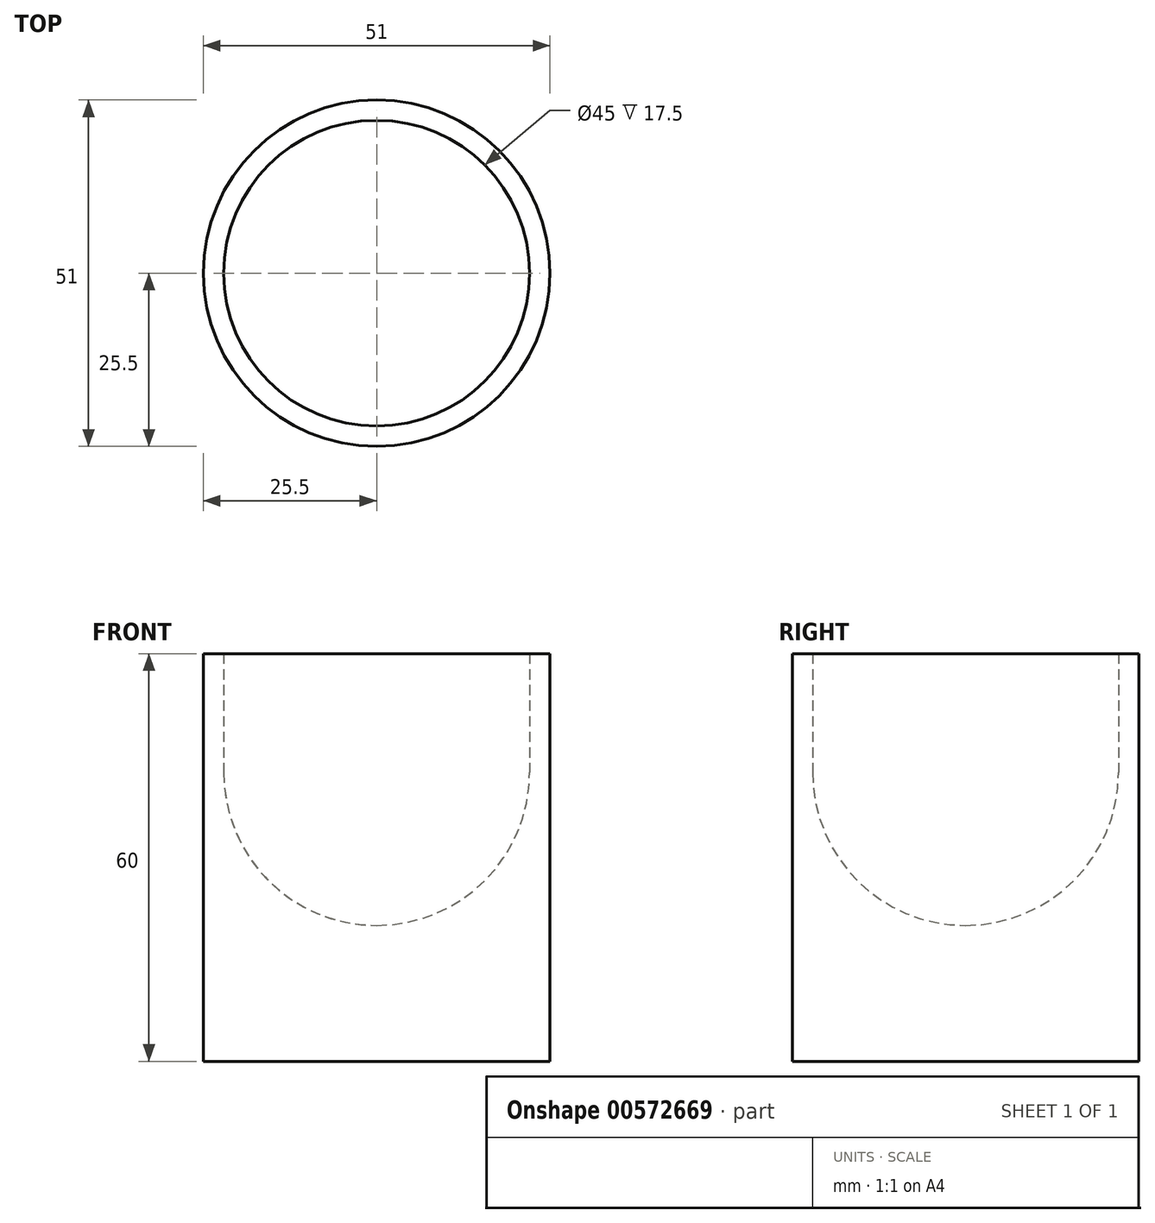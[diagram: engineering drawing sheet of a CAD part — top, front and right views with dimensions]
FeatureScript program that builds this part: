
annotation { "Feature Type Name" : "Feature", "Feature Type Description" : "" }
export const myFeature = defineFeature(function(context is Context, id is Id, definition is map)
    precondition{}
    {
        {
            var Q0;
            Q0=qCreatedBy(makeId("Front.planeOp"),FACE);
            var sketch = newSketch(context, id + "F0", { "sketchPlane" : qUnion([Q0])});
            skCircle(sketch, "E0", {"center": v(0, 0) * mm, "radius": 22.5 * mm});
            skLineSegment(sketch, "E1", {"start": v(-22.5, 0) * mm, "end": v(-22.5, 17.5) * mm});
            skLineSegment(sketch, "E2", {"start": v(-22.5, 17.5) * mm, "end": v(-25.5, 17.5) * mm});
            skLineSegment(sketch, "E3", {"start": v(-25.5, 17.5) * mm, "end": v(-25.5, -42.5) * mm});
            skLineSegment(sketch, "E4", {"start": v(-25.5, -42.5) * mm, "end": v(0, -42.5) * mm});
            skLineSegment(sketch, "E5", {"start": v(0, -42.5) * mm, "end": v(0, -22.5) * mm});
            skSolve(sketch);
        }
        {
            var Q0;
            {var subQ0=sQuery(id+"F0.wireOp",EDGE,"E1");Q0=makeQuery(id+"F0.imprint","IMPRINT",FACE,{"disambiguationData":[TD([[makeQuery(id+"F0.imprint","IMPRINT",EDGE,{"derivedFrom":subQ0}),1.0]])]});}
            var Q1;
            Q1=sQuery(id+"F0.wireOp",EDGE,"E5");
            revolve(context, id + "F1", {"entities" : qUnion([Q0]), "axis" : qUnion([Q1]), "revolveType" : RevolveType.FULL});
        }
    });
